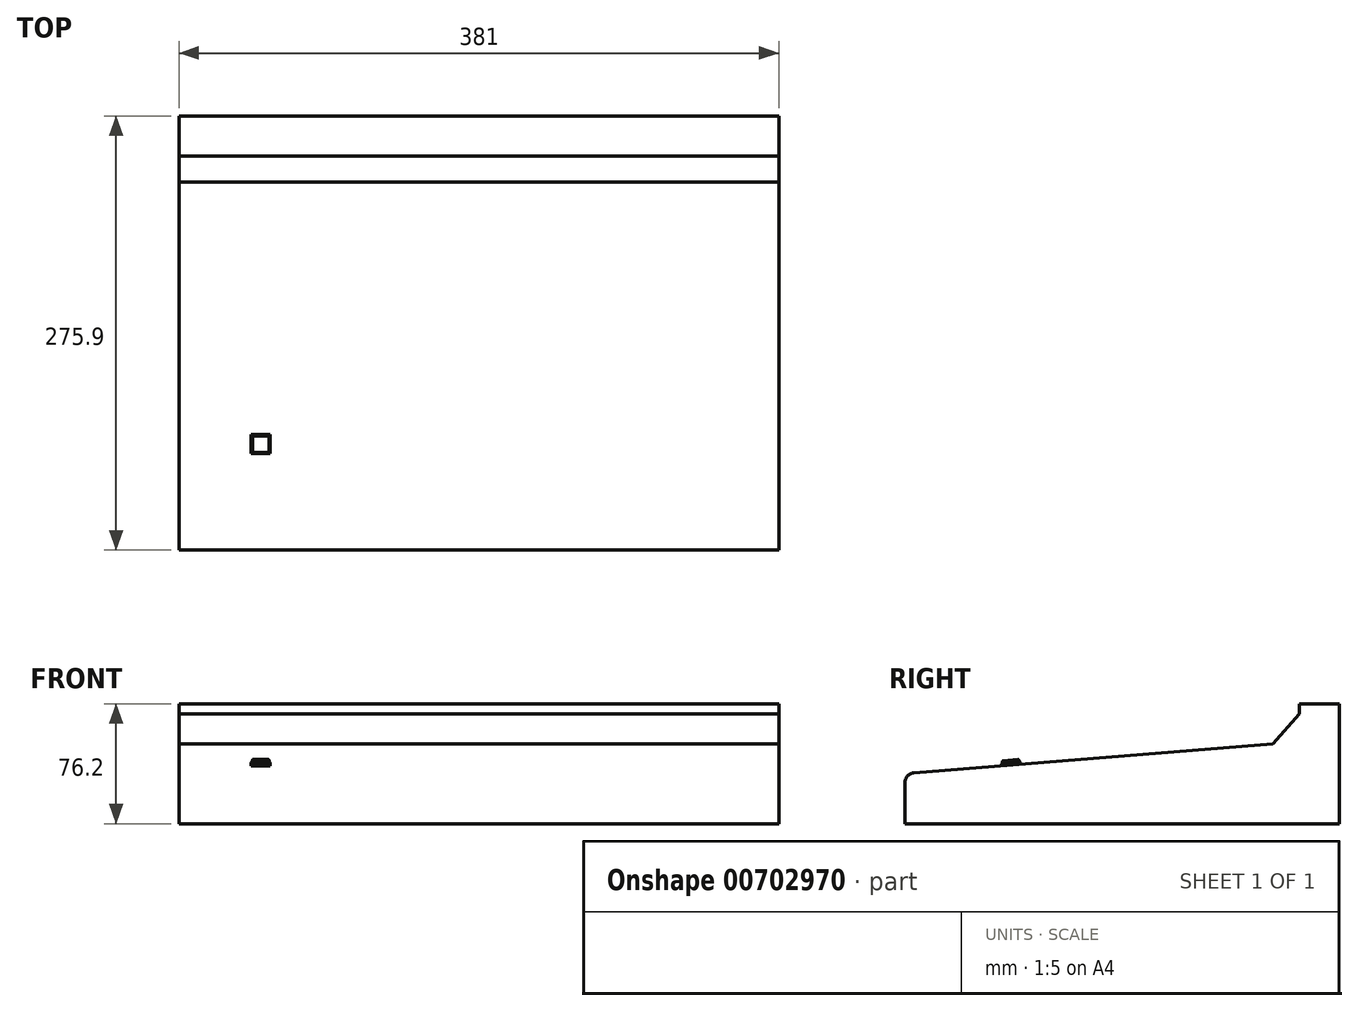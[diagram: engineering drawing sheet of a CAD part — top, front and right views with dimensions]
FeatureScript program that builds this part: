
annotation { "Feature Type Name" : "Feature", "Feature Type Description" : "" }
export const myFeature = defineFeature(function(context is Context, id is Id, definition is map)
    precondition{}
    {
        {
            var Q0;
            Q0=qCreatedBy(makeId("Right.planeOp"),FACE);
            var sketch = newSketch(context, id + "F0", { "sketchPlane" : qUnion([Q0])});
            skLineSegment(sketch, "E0", {"start": v(111.12, -76.2) * mm, "end": v(-164.78, -76.2) * mm});
            skLineSegment(sketch, "E1", {"start": v(-164.78, -76.2) * mm, "end": v(-164.78, -50.2) * mm});
            skLineSegment(sketch, "E2", {"start": v(-158.94, -43.87) * mm, "end": v(68.91, -25.4) * mm});
            skLineSegment(sketch, "E3", {"start": v(68.91, -25.4) * mm, "end": v(85.72, -6.36) * mm});
            skLineSegment(sketch, "E4", {"start": v(85.72, -6.36) * mm, "end": v(85.72, 0) * mm});
            skLineSegment(sketch, "E5", {"start": v(85.72, 0) * mm, "end": v(111.12, 0) * mm});
            skLineSegment(sketch, "E6", {"start": v(111.12, 0) * mm, "end": v(111.12, -76.2) * mm});
            skPoint(sketch, "E7.visualSharp", {"position": v(-164.78, -44.35) * mm});
            skArc(sketch, "E7.filletArc", {"start": v(-158.94, -43.87) * mm, "mid": v(-163.1, -45.9) * mm, "end": v(-164.78, -50.2) * mm});
            skSolve(sketch);
        }
        {
            var Q0;
            Q0=makeQuery(id+"F0.imprint","IMPRINT",FACE,{"disambiguationData":[TD([[makeQuery(id+"F0.imprint","IMPRINT",EDGE,{"derivedFrom":sQuery(id+"F0.wireOp",EDGE,"E0")}),-1.0]])]});
            extrude(context, id + "F1", {"entities" : qUnion([Q0]), "endBound" : BoundingType.SYMMETRIC, "depth" : 381 * mm, "offsetDistance" : 25.4 * mm});
        }
        {
            var Q0;
            Q0=makeQuery(id+"F1.opExtrude","SWEPT_FACE",FACE,{"disambiguationData":[OSD([sQuery(id+"F0.wireOp",EDGE,"E2")])]});
            var sketch = newSketch(context, id + "F2", { "sketchPlane" : qUnion([Q0])});
            skLineSegment(sketch, "E8.bottom", {"start": v(-144.61, -94.2) * mm, "end": v(-132.61, -94.2) * mm});
            skLineSegment(sketch, "E8.top", {"start": v(-144.61, -106.2) * mm, "end": v(-132.61, -106.2) * mm});
            skLineSegment(sketch, "E8.left", {"start": v(-144.61, -94.2) * mm, "end": v(-144.61, -106.2) * mm});
            skLineSegment(sketch, "E8.right", {"start": v(-132.61, -94.2) * mm, "end": v(-132.61, -106.2) * mm});
            skSolve(sketch);
        }
        {
            var Q0;
            Q0=makeQuery(id+"F2.imprint","IMPRINT",FACE,{"disambiguationData":[TD([[makeQuery(id+"F2.imprint","IMPRINT",EDGE,{"derivedFrom":sQuery(id+"F2.wireOp",EDGE,"E8.bottom")}),-1.0]])]});
            extrude(context, id + "F3", {"entities" : qUnion([Q0]), "operationType" : NewBodyOperationType.ADD, "depth" : 2 * mm, "offsetDistance" : 25 * mm});
        }
        {
            var Q0;
            Q0=makeQuery(id+"F3.opExtrude","CAP_FACE",FACE,{"disambiguationData":[OSD([sQuery(id+"F2.wireOp",EDGE,"E8.bottom"),sQuery(id+"F2.wireOp",EDGE,"E8.top"),sQuery(id+"F2.wireOp",EDGE,"E8.left"),sQuery(id+"F2.wireOp",EDGE,"E8.right")])],"isStart":false});
            chamfer(context, id + "F4", {"entities" : qUnion([Q0]), "width" : .8 * mm, "tangentPropagation" : true});
        }
        {
            var Q0;
            Q0=makeQuery(id+"F3.opExtrude","CAP_FACE",FACE,{"disambiguationData":[OSD([sQuery(id+"F2.wireOp",EDGE,"E8.bottom"),sQuery(id+"F2.wireOp",EDGE,"E8.top"),sQuery(id+"F2.wireOp",EDGE,"E8.left"),sQuery(id+"F2.wireOp",EDGE,"E8.right")])],"isStart":false});
            extrude(context, id + "F5", {"entities" : qUnion([Q0]), "operationType" : NewBodyOperationType.ADD, "depth" : 1 * mm, "offsetDistance" : 25 * mm});
        }
        {
            var Q0;
            Q0=makeQuery(id+"F5.opExtrude","CAP_FACE",FACE,{"disambiguationData":[OSD([sQuery(id+"F2.wireOp",EDGE,"E8.bottom"),sQuery(id+"F2.wireOp",EDGE,"E8.top"),sQuery(id+"F2.wireOp",EDGE,"E8.left"),sQuery(id+"F2.wireOp",EDGE,"E8.right")])],"isStart":false});
            fillet(context, id + "F6", {"entities" : qUnion([Q0]), "radius" : .4 * mm, "tangentPropagation" : true, "allowEdgeOverflow" : false});
        }
    });
